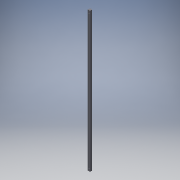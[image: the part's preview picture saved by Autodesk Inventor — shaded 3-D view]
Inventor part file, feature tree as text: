
AUTODESK INVENTOR PART (.ipt)
format: ipt  version: 2016 SP1 (Build 200210100, 210)  size: 148,992 bytes
history: native  units: mm (DEFAULTED — no unit token found)
features: other x2, sketch x2, extrude x1, hole x1, pattern_linear x1
ambient origin geometry x8: Origin, YZ Plane, XZ Plane, XY Plane, X Axis, Y Axis, Z Axis, Center Point
bodies: Solid1 (feature_tree)
feature tree (7):
  other  "Table"
  other  "HSR20-xxxx-01"
  extrude  "Extrusion4"  Depth=20.0mm
  hole  "Hole1"  [1 undecoded]
  pattern_linear  "Rectangular Pattern1"  [2 undecoded]
  sketch  "Sketch4"  dims[d6=1060.0mm d7=0.0mm d8=20.0mm]
  sketch  "Sketch5"  dims[d9=6.0mm d10=6.0mm d11=9.5mm d12=8.5mm d13=90.0deg d14=8.0mm d15=20.594885mm d16=20.0mm d18=1020.0mm]
note: 3 required parameter values undecoded (feature->parameter linkage not recoverable at this tier; creation-order binding heuristic only, values carry confidence <= 0.55)
